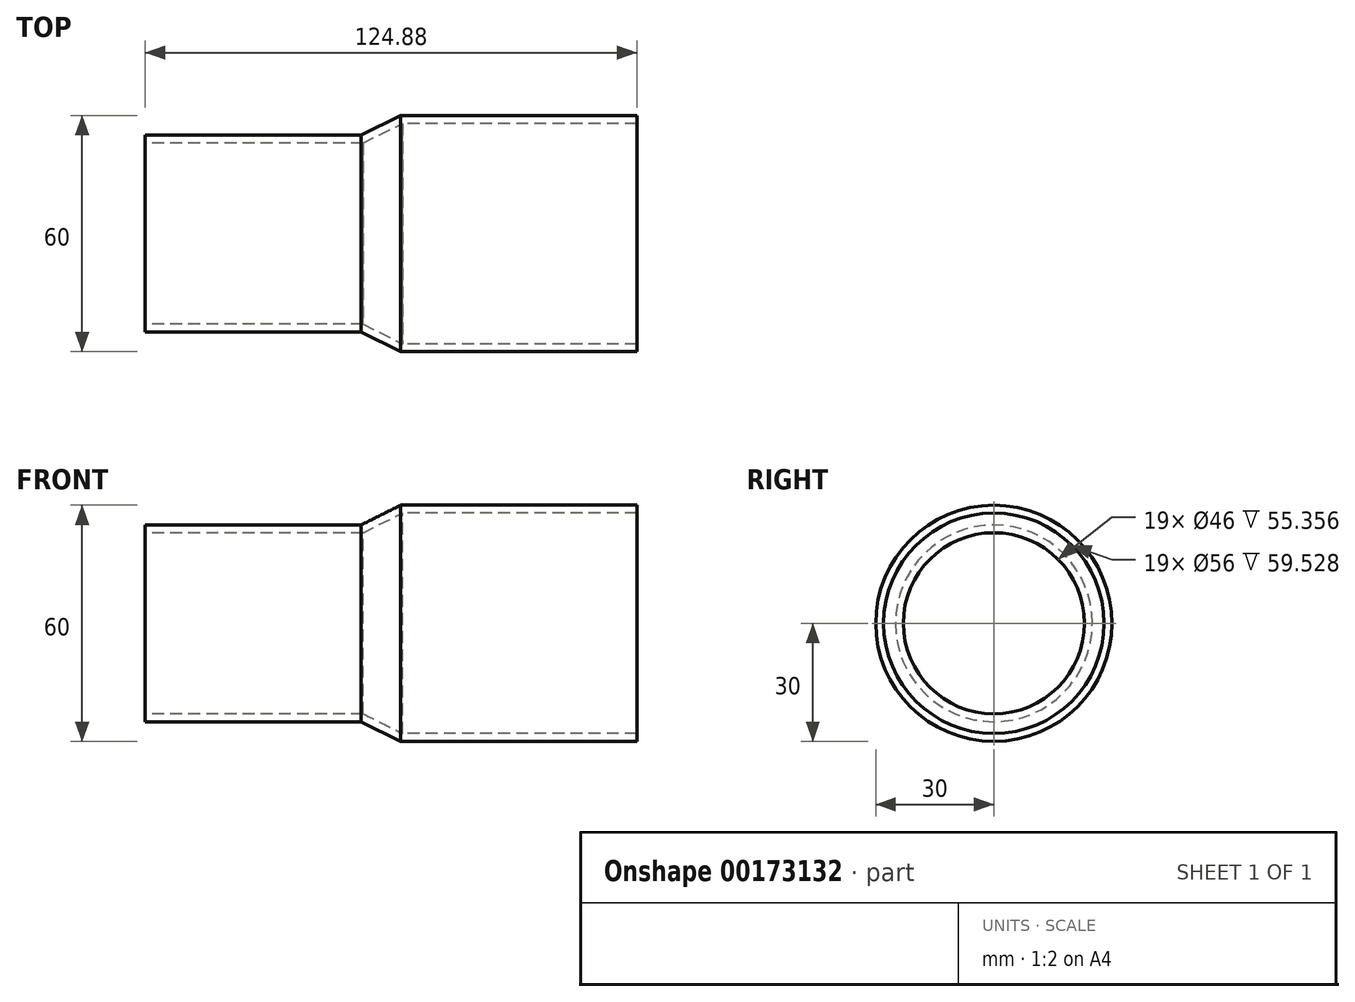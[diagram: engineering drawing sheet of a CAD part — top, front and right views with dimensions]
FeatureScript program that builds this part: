
annotation { "Feature Type Name" : "Feature", "Feature Type Description" : "" }
export const myFeature = defineFeature(function(context is Context, id is Id, definition is map)
    precondition{}
    {
        {
            var Q0;
            Q0=qCreatedBy(makeId("Front.planeOp"),FACE);
            var sketch = newSketch(context, id + "F0", { "sketchPlane" : qUnion([Q0])});
            skLineSegment(sketch, "E0", {"start": v(47.75, 30) * mm, "end": v(-12.25, 30) * mm});
            skLineSegment(sketch, "E1", {"start": v(-77.13, 25) * mm, "end": v(-22.25, 25) * mm});
            skLineSegment(sketch, "E2", {"start": v(-88.45, 0) * mm, "end": v(78, 0) * mm});
            skLineSegment(sketch, "E3", {"start": v(-22.25, 25) * mm, "end": v(-12.25, 30) * mm});
            skLineSegment(sketch, "E4", {"start": v(-77.13, 25) * mm, "end": v(-77.13, 0) * mm});
            skLineSegment(sketch, "E5", {"start": v(47.75, 30) * mm, "end": v(47.75, 0) * mm});
            skSolve(sketch);
        }
        {
            var Q0;
            Q0=makeQuery(id+"F0.imprint","IMPRINT",FACE,{"disambiguationData":[TD([[makeQuery(id+"F0.imprint","IMPRINT",EDGE,{"derivedFrom":sQuery(id+"F0.wireOp",EDGE,"E0")}),1.0]])]});
            var Q1;
            Q1=sQuery(id+"F0.wireOp",EDGE,"E2");
            revolve(context, id + "F4", {"entities" : qUnion([Q0]), "axis" : qUnion([Q1]), "revolveType" : RevolveType.FULL});
        }
        {
            var Q0;
            Q0=makeQuery(id+"F4.opRevolve","SWEPT_FACE",FACE,{"disambiguationData":[OSD([sQuery(id+"F0.wireOp",EDGE,"E4")])]});
            shell(context, id + "F1", {"entities" : qUnion([Q0]), "thickness" : 2 * mm});
        }
        {
            var Q0;
            Q0=makeQuery(id+"F1.opShell","OFFSET_FACE",FACE,{"disambiguationData":[OSD([sQuery(id+"F0.wireOp",EDGE,"E5")])]});
            var sketch = newSketch(context, id + "F2", { "sketchPlane" : qUnion([Q0])});
            skCircle(sketch, "E6.0", {"center": v(0, 0) * mm, "radius": 28 * mm});
            skSolve(sketch);
        }
        {
            var Q0;
            Q0=makeQuery(id+"F2.imprint","IMPRINT",FACE,{"disambiguationData":[TD([[makeQuery(id+"F2.imprint","IMPRINT",EDGE,{"derivedFrom":sQuery(id+"F2.wireOp",EDGE,"E6.0")}),1.0]])]});
            extrude(context, id + "F3", {"entities" : qUnion([Q0]), "operationType" : NewBodyOperationType.REMOVE, "oppositeDirection" : true, "depth" : 25 * mm});
        }
    });
